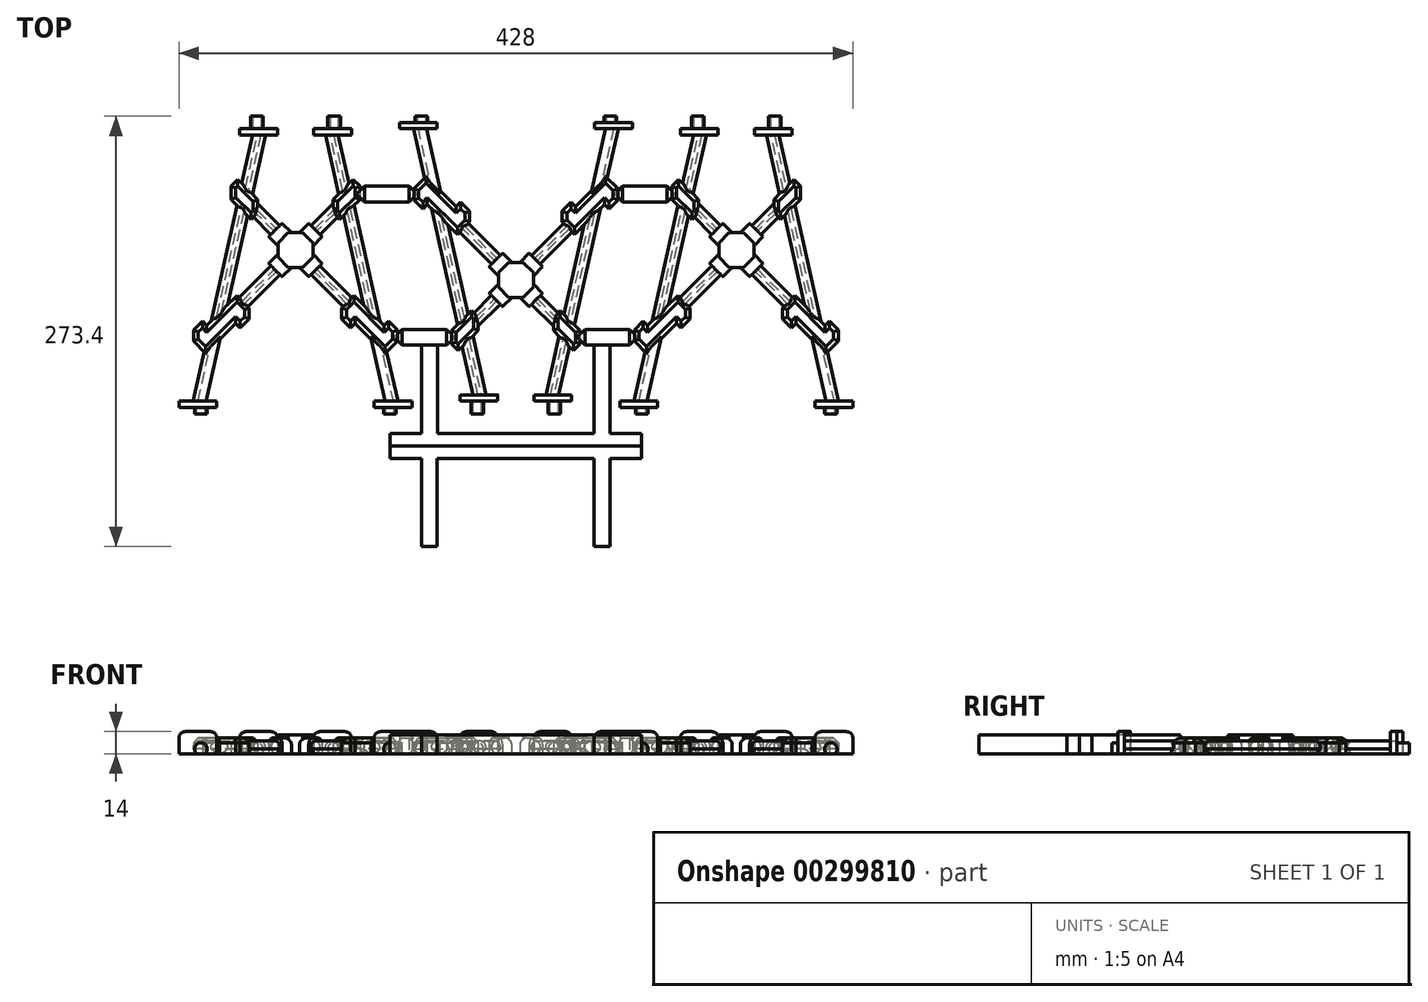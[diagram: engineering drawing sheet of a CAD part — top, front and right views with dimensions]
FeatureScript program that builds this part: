
annotation { "Feature Type Name" : "Feature", "Feature Type Description" : "" }
export const myFeature = defineFeature(function(context is Context, id is Id, definition is map)
    precondition{}
    {
        {
            var Q0;
            Q0=qCreatedBy(makeId("Front.planeOp"),FACE);
            var sketch = newSketch(context, id + "F0", { "sketchPlane" : qUnion([Q0])});
            skLineSegment(sketch, "E0", {"start": v(0, 0) * mm, "end": v(0, 65.95) * mm});
            skSolve(sketch);
        }
        {
            var Q0;
            Q0=qCreatedBy(makeId("Top.planeOp"),FACE);
            var sketch = newSketch(context, id + "F1", { "sketchPlane" : qUnion([Q0])});
            skLineSegment(sketch, "E1", {"start": v(26.5, 176.13) * mm, "end": v(65.92, 0) * mm});
            skLineSegment(sketch, "E2", {"start": v(18.1, 177) * mm, "end": v(27.88, 133.35) * mm});
            skLineSegment(sketch, "E3", {"start": v(43.95, 61.52) * mm, "end": v(5.66, 99.81) * mm});
            skLineSegment(sketch, "E4", {"start": v(47.21, 46.95) * mm, "end": v(0, 94.16) * mm});
            skLineSegment(sketch, "E5", {"start": v(43.95, 61.52) * mm, "end": v(57.71, 0.03) * mm});
            skLineSegment(sketch, "E6", {"start": v(5.66, 99.81) * mm, "end": v(29.95, 124.1) * mm});
            skLineSegment(sketch, "E7", {"start": v(0, 105.47) * mm, "end": v(27.88, 133.35) * mm});
            skLineSegment(sketch, "E8", {"start": v(0, 94.16) * mm, "end": v(0, 105.47) * mm});
            skLineSegment(sketch, "E9", {"start": v(18.1, 177) * mm, "end": v(26.5, 176.13) * mm});
            skLineSegment(sketch, "E10", {"start": v(57.71, 0.03) * mm, "end": v(65.92, 0) * mm});
            skLineSegment(sketch, "E11.trimOffspring", {"start": v(29.95, 124.1) * mm, "end": v(43.95, 61.52) * mm});
            skLineSegment(sketch, "E12.trimOffspring", {"start": v(47.21, 46.95) * mm, "end": v(57.71, 0.03) * mm});
            skLineSegment(sketch, "E13.MirrorCS", {"start": v(-43.95, 61.52) * mm, "end": v(-5.66, 99.81) * mm});
            skLineSegment(sketch, "E14.MirrorCS", {"start": v(-47.21, 46.95) * mm, "end": v(0, 94.16) * mm});
            skLineSegment(sketch, "E15.MirrorCS", {"start": v(-47.21, 46.95) * mm, "end": v(-57.71, 0.03) * mm});
            skLineSegment(sketch, "E16.MirrorCS", {"start": v(-18.1, 177) * mm, "end": v(-26.5, 176.13) * mm});
            skLineSegment(sketch, "E17.MirrorCS", {"start": v(-26.5, 176.13) * mm, "end": v(-65.92, 0) * mm});
            skLineSegment(sketch, "E18.MirrorCS", {"start": v(-18.1, 177) * mm, "end": v(-27.88, 133.35) * mm});
            skLineSegment(sketch, "E19.MirrorCS", {"start": v(-43.95, 61.52) * mm, "end": v(-57.71, 0.03) * mm});
            skLineSegment(sketch, "E20.MirrorCS", {"start": v(-5.66, 99.81) * mm, "end": v(-29.95, 124.1) * mm});
            skLineSegment(sketch, "E21.MirrorCS", {"start": v(0, 105.47) * mm, "end": v(-27.88, 133.35) * mm});
            skLineSegment(sketch, "E22.MirrorCS", {"start": v(-57.71, 0.03) * mm, "end": v(-65.92, 0) * mm});
            skLineSegment(sketch, "E23.MirrorCS", {"start": v(-29.95, 124.1) * mm, "end": v(-43.95, 61.52) * mm});
            skSolve(sketch);
        }
        {
            var Q0;
            Q0 = qSketchRegion(id + "F1", true);
            extrude(context, id + "F2", {"entities" : qUnion([Q0]), "depth" : 8 * mm});
        }
        {
            var Q0;
            Q0=qCreatedBy(makeId("Top.planeOp"),FACE);
            var sketch = newSketch(context, id + "F3", { "sketchPlane" : qUnion([Q0])});
            skLineSegment(sketch, "E24", {"start": v(0, 0) * mm, "end": v(50, 0) * mm});
            skLineSegment(sketch, "E25.bottom", {"start": v(50, 0) * mm, "end": v(74, 0) * mm});
            skLineSegment(sketch, "E25.top", {"start": v(50, 4) * mm, "end": v(74, 4) * mm});
            skLineSegment(sketch, "E25.left", {"start": v(50, 0) * mm, "end": v(50, 4) * mm});
            skLineSegment(sketch, "E25.right", {"start": v(74, 0) * mm, "end": v(74, 4) * mm});
            skLineSegment(sketch, "E26", {"start": v(0, 0) * mm, "end": v(0, 177) * mm});
            skLineSegment(sketch, "E27", {"start": v(0, 177) * mm, "end": v(11.5, 177) * mm});
            skLineSegment(sketch, "E28.bottom", {"start": v(11.5, 177) * mm, "end": v(35.5, 177) * mm});
            skLineSegment(sketch, "E28.top", {"start": v(11.5, 173) * mm, "end": v(35.5, 173) * mm});
            skLineSegment(sketch, "E28.left", {"start": v(11.5, 177) * mm, "end": v(11.5, 173) * mm});
            skLineSegment(sketch, "E28.right", {"start": v(35.5, 177) * mm, "end": v(35.5, 173) * mm});
            skLineSegment(sketch, "E29.MirrorCS", {"start": v(-11.5, 177) * mm, "end": v(-35.5, 177) * mm});
            skLineSegment(sketch, "E30.MirrorCS", {"start": v(-11.5, 173) * mm, "end": v(-35.5, 173) * mm});
            skLineSegment(sketch, "E31.MirrorCS", {"start": v(-35.5, 177) * mm, "end": v(-35.5, 173) * mm});
            skLineSegment(sketch, "E32.MirrorCS", {"start": v(-11.5, 177) * mm, "end": v(-11.5, 173) * mm});
            skLineSegment(sketch, "E33.MirrorCS", {"start": v(-50, 0) * mm, "end": v(-50, 4) * mm});
            skLineSegment(sketch, "E34.MirrorCS", {"start": v(-50, 0) * mm, "end": v(-74, 0) * mm});
            skLineSegment(sketch, "E35.MirrorCS", {"start": v(-50, 4) * mm, "end": v(-74, 4) * mm});
            skLineSegment(sketch, "E36.MirrorCS", {"start": v(-74, 0) * mm, "end": v(-74, 4) * mm});
            skSolve(sketch);
        }
        {
            var Q0;
            Q0 = qSketchRegion(id + "F3", true);
            extrude(context, id + "F4", {"entities" : qUnion([Q0]), "operationType" : NewBodyOperationType.ADD, "depth" : 14 * mm});
        }
        {
            var Q0;
            Q0=makeQuery(id+"F4.opExtrude","SWEPT_FACE",FACE,{"disambiguationData":[OSD([sQuery(id+"F3.wireOp",EDGE,"E25.bottom")])]});
            var sketch = newSketch(context, id + "F5", { "sketchPlane" : qUnion([Q0])});
            skPoint(sketch, "E37.endSnap0", {"position": v(50, 7) * mm});
            skLineSegment(sketch, "E38", {"start": v(60, 0) * mm, "end": v(60, 3) * mm});
            skArc(sketch, "E39", {"start": v(62.65, 0) * mm, "mid": v(60, 7) * mm, "end": v(57.35, 0) * mm});
            skLineSegment(sketch, "E40", {"start": v(57.35, 0) * mm, "end": v(62.65, 0) * mm});
            skLineSegment(sketch, "E41.MirrorCS", {"start": v(-57.35, 0) * mm, "end": v(-62.65, 0) * mm});
            skLineSegment(sketch, "E42.MirrorCS", {"start": v(-60, 0) * mm, "end": v(-60, 3) * mm});
            skArc(sketch, "E43.MirrorCS", {"start": v(-62.65, 0) * mm, "mid": v(-60, 7) * mm, "end": v(-57.35, 0) * mm});
            skPoint(sketch, "E44.MirrorP", {"position": v(-50, 7) * mm});
            skSolve(sketch);
        }
        {
            var Q0;
            Q0 = qSketchRegion(id + "F5", true);
            extrude(context, id + "F6", {"entities" : qUnion([Q0]), "operationType" : NewBodyOperationType.ADD, "depth" : 4 * mm});
        }
        {
            var Q0;
            Q0=makeQuery(id+"F4.opExtrude","SWEPT_FACE",FACE,{"disambiguationData":[OSD([sQuery(id+"F3.wireOp",EDGE,"E29.MirrorCS")])]});
            var sketch = newSketch(context, id + "F7", { "sketchPlane" : qUnion([Q0])});
            skArc(sketch, "E45", {"start": v(27.15, 0) * mm, "mid": v(24.5, 7) * mm, "end": v(21.85, 0) * mm});
            skLineSegment(sketch, "E46", {"start": v(21.85, 0) * mm, "end": v(27.15, 0) * mm});
            skArc(sketch, "E47.MirrorCS", {"start": v(-27.15, 0) * mm, "mid": v(-24.5, 7) * mm, "end": v(-21.85, 0) * mm});
            skLineSegment(sketch, "E48.MirrorCS", {"start": v(-21.85, 0) * mm, "end": v(-27.15, 0) * mm});
            skSolve(sketch);
        }
        {
            var Q0;
            Q0 = qSketchRegion(id + "F7", true);
            extrude(context, id + "F8", {"entities" : qUnion([Q0]), "operationType" : NewBodyOperationType.ADD, "depth" : 8 * mm});
        }
        {
            var Q0;
            Q0=qCreatedBy(makeId("Top.planeOp"),FACE);
            var sketch = newSketch(context, id + "F9", { "sketchPlane" : qUnion([Q0])});
            skLineSegment(sketch, "E49.bottom", {"start": v(8.49, 83.04) * mm, "end": v(0, 91.52) * mm});
            skLineSegment(sketch, "E49.top", {"start": v(16.97, 91.52) * mm, "end": v(8.49, 100) * mm});
            skLineSegment(sketch, "E49.left", {"start": v(8.49, 83.04) * mm, "end": v(16.97, 91.52) * mm});
            skLineSegment(sketch, "E49.right", {"start": v(-16.97, 108.5) * mm, "end": v(-8.49, 116.98) * mm});
            skPoint(sketch, "E49.middle", {"position": v(0, 100) * mm});
            skLineSegment(sketch, "E50.bottom", {"start": v(16.97, 108.5) * mm, "end": v(8.49, 116.98) * mm});
            skLineSegment(sketch, "E50.top", {"start": v(-8.49, 83.04) * mm, "end": v(-16.97, 91.52) * mm});
            skLineSegment(sketch, "E50.left", {"start": v(16.97, 108.5) * mm, "end": v(8.49, 100) * mm});
            skLineSegment(sketch, "E50.right", {"start": v(8.49, 116.98) * mm, "end": v(0, 108.5) * mm});
            skLineSegment(sketch, "E51.trimOffspring", {"start": v(0, 108.5) * mm, "end": v(-8.49, 116.98) * mm});
            skLineSegment(sketch, "E52.trimOffspring", {"start": v(-8.49, 100) * mm, "end": v(-16.97, 91.52) * mm});
            skLineSegment(sketch, "E53.trimOffspring", {"start": v(-8.49, 100) * mm, "end": v(-16.97, 108.5) * mm});
            skLineSegment(sketch, "E54.trimOffspring", {"start": v(0, 91.52) * mm, "end": v(-8.49, 83.04) * mm});
            skSolve(sketch);
        }
        {
            var Q0;
            Q0 = qSketchRegion(id + "F9", true);
            extrude(context, id + "F10", {"entities" : qUnion([Q0]), "operationType" : NewBodyOperationType.ADD, "depth" : 10 * mm});
        }
        {
            var Q0;
            Q0=qCreatedBy(makeId("Top.planeOp"),FACE);
            var sketch = newSketch(context, id + "F11", { "sketchPlane" : qUnion([Q0])});
            skLineSegment(sketch, "E55.bottom", {"start": v(35.07, 50.59) * mm, "end": v(29.41, 56.25) * mm});
            skLineSegment(sketch, "E55.top", {"start": v(64.77, 49.18) * mm, "end": v(59.11, 54.83) * mm});
            skLineSegment(sketch, "E55.right", {"start": v(29.41, 63.32) * mm, "end": v(37.2, 71.1) * mm});
            skPoint(sketch, "E55.middle", {"position": v(42.38, 57.42) * mm});
            skLineSegment(sketch, "E56", {"start": v(64.77, 42.1) * mm, "end": v(64.77, 49.18) * mm});
            skLineSegment(sketch, "E57", {"start": v(29.41, 56.25) * mm, "end": v(29.41, 63.32) * mm});
            skLineSegment(sketch, "E58", {"start": v(59.11, 54.83) * mm, "end": v(56.29, 52) * mm});
            skLineSegment(sketch, "E59", {"start": v(56.29, 52) * mm, "end": v(37.2, 71.1) * mm});
            skLineSegment(sketch, "E60", {"start": v(29.41, 56.25) * mm, "end": v(35.07, 50.59) * mm});
            skLineSegment(sketch, "E61", {"start": v(35.07, 50.59) * mm, "end": v(37.9, 53.42) * mm});
            skLineSegment(sketch, "E62", {"start": v(37.9, 53.42) * mm, "end": v(57, 34.33) * mm});
            skPoint(sketch, "E63.orphan", {"position": v(25.88, 59.78) * mm});
            skPoint(sketch, "E64.orphan", {"position": v(40.02, 73.92) * mm});
            skPoint(sketch, "E65.orphan", {"position": v(44.74, 40.93) * mm});
            skLineSegment(sketch, "E66", {"start": v(57, 34.33) * mm, "end": v(64.77, 42.1) * mm});
            skLineSegment(sketch, "E67.MirrorCS", {"start": v(-59.11, 54.83) * mm, "end": v(-56.29, 52) * mm});
            skLineSegment(sketch, "E68.MirrorCS", {"start": v(-35.07, 50.59) * mm, "end": v(-37.9, 53.42) * mm});
            skLineSegment(sketch, "E69.MirrorCS", {"start": v(-64.77, 49.18) * mm, "end": v(-59.11, 54.83) * mm});
            skLineSegment(sketch, "E70.MirrorCS", {"start": v(-35.07, 50.59) * mm, "end": v(-29.41, 56.25) * mm});
            skLineSegment(sketch, "E71.MirrorCS", {"start": v(-29.41, 56.25) * mm, "end": v(-29.41, 63.32) * mm});
            skPoint(sketch, "E72.MirrorP", {"position": v(-25.88, 59.78) * mm});
            skPoint(sketch, "E73.MirrorP", {"position": v(-42.38, 57.42) * mm});
            skLineSegment(sketch, "E74.MirrorCS", {"start": v(-37.9, 53.42) * mm, "end": v(-57, 34.33) * mm});
            skPoint(sketch, "E75.MirrorP", {"position": v(-40.02, 73.92) * mm});
            skPoint(sketch, "E76.MirrorP", {"position": v(-44.74, 40.93) * mm});
            skLineSegment(sketch, "E77.MirrorCS", {"start": v(-64.77, 42.1) * mm, "end": v(-64.77, 49.18) * mm});
            skLineSegment(sketch, "E78.MirrorCS", {"start": v(-29.41, 56.25) * mm, "end": v(-35.07, 50.59) * mm});
            skLineSegment(sketch, "E79.MirrorCS", {"start": v(-29.41, 63.32) * mm, "end": v(-37.2, 71.1) * mm});
            skLineSegment(sketch, "E80.MirrorCS", {"start": v(-57, 34.33) * mm, "end": v(-64.77, 42.1) * mm});
            skLineSegment(sketch, "E81.MirrorCS", {"start": v(-56.29, 52) * mm, "end": v(-37.2, 71.1) * mm});
            skSolve(sketch);
        }
        {
            var Q0;
            Q0 = qSketchRegion(id + "F11", true);
            extrude(context, id + "F12", {"entities" : qUnion([Q0]), "operationType" : NewBodyOperationType.ADD, "depth" : 10 * mm});
        }
        {
            var Q0;
            Q0=qCreatedBy(makeId("Top.planeOp"),FACE);
            var sketch = newSketch(context, id + "F13", { "sketchPlane" : qUnion([Q0])});
            skLineSegment(sketch, "E82", {"start": v(23.9, 132.15) * mm, "end": v(36.63, 144.88) * mm});
            skLineSegment(sketch, "E83", {"start": v(23.9, 123.67) * mm, "end": v(28.15, 119.43) * mm});
            skLineSegment(sketch, "E84", {"start": v(28.15, 119.43) * mm, "end": v(40.87, 132.15) * mm});
            skLineSegment(sketch, "E85", {"start": v(40.87, 140.64) * mm, "end": v(36.63, 144.88) * mm});
            skLineSegment(sketch, "E86", {"start": v(40.87, 140.64) * mm, "end": v(40.87, 132.15) * mm});
            skLineSegment(sketch, "E87", {"start": v(23.9, 123.67) * mm, "end": v(23.9, 132.15) * mm});
            skPoint(sketch, "E88.orphan", {"position": v(45.12, 136.4) * mm});
            skPoint(sketch, "E89.orphan", {"position": v(19.66, 127.91) * mm});
            skLineSegment(sketch, "E90.MirrorCS", {"start": v(-23.9, 123.67) * mm, "end": v(-23.9, 132.15) * mm});
            skPoint(sketch, "E91.MirrorP", {"position": v(-45.12, 136.4) * mm});
            skPoint(sketch, "E92.MirrorP", {"position": v(-19.66, 127.91) * mm});
            skLineSegment(sketch, "E93.MirrorCS", {"start": v(-40.87, 140.64) * mm, "end": v(-40.87, 132.15) * mm});
            skLineSegment(sketch, "E94.MirrorCS", {"start": v(-28.15, 119.43) * mm, "end": v(-40.87, 132.15) * mm});
            skLineSegment(sketch, "E95.MirrorCS", {"start": v(-23.9, 132.15) * mm, "end": v(-36.63, 144.88) * mm});
            skLineSegment(sketch, "E96.MirrorCS", {"start": v(-23.9, 123.67) * mm, "end": v(-28.15, 119.43) * mm});
            skLineSegment(sketch, "E97.MirrorCS", {"start": v(-40.87, 140.64) * mm, "end": v(-36.63, 144.88) * mm});
            skSolve(sketch);
        }
        {
            var Q0;
            Q0 = qSketchRegion(id + "F13", true);
            extrude(context, id + "F14", {"entities" : qUnion([Q0]), "operationType" : NewBodyOperationType.ADD, "depth" : 10 * mm});
        }
        {
            var Q0;
            {var subQ0=sQuery(id+"F1.wireOp",EDGE,"E17.MirrorCS");Q0=makeQuery(id+"F12.boolean.opBoolean","SPLIT",EDGE,{"disambiguationData":[TD([makeQuery(id+"F4.opExtrude","SWEPT_FACE",FACE,{"disambiguationData":[OSD([sQuery(id+"F3.wireOp",EDGE,"E30.MirrorCS")])]})])],"derivedFrom":makeQuery(id+"F2.opExtrude","CAP_EDGE",EDGE,{"disambiguationData":[OSD([subQ0])],"isStart":false})});}
            var Q1;
            Q1=makeQuery(id+"F2.opExtrude","CAP_EDGE",EDGE,{"disambiguationData":[OSD([sQuery(id+"F1.wireOp",EDGE,"E23.MirrorCS")])],"isStart":false});
            var Q2;
            Q2=makeQuery(id+"F2.opExtrude","CAP_EDGE",EDGE,{"disambiguationData":[OSD([sQuery(id+"F1.wireOp",EDGE,"E18.MirrorCS")])],"isStart":false});
            var Q3;
            Q3=makeQuery(id+"F2.opExtrude","CAP_EDGE",EDGE,{"disambiguationData":[OSD([sQuery(id+"F1.wireOp",EDGE,"E21.MirrorCS")])],"isStart":false});
            var Q4;
            Q4=makeQuery(id+"F2.opExtrude","CAP_EDGE",EDGE,{"disambiguationData":[OSD([sQuery(id+"F1.wireOp",EDGE,"E20.MirrorCS")])],"isStart":false});
            var Q5;
            Q5=makeQuery(id+"F2.opExtrude","CAP_EDGE",EDGE,{"disambiguationData":[OSD([sQuery(id+"F1.wireOp",EDGE,"E7")])],"isStart":false});
            var Q6;
            Q6=makeQuery(id+"F2.opExtrude","CAP_EDGE",EDGE,{"disambiguationData":[OSD([sQuery(id+"F1.wireOp",EDGE,"E2")])],"isStart":false});
            var Q7;
            {var subQ0=sQuery(id+"F1.wireOp",EDGE,"E1");Q7=makeQuery(id+"F12.boolean.opBoolean","SPLIT",EDGE,{"disambiguationData":[TD([makeQuery(id+"F4.opExtrude","SWEPT_FACE",FACE,{"disambiguationData":[OSD([sQuery(id+"F3.wireOp",EDGE,"E28.top")])]})])],"derivedFrom":makeQuery(id+"F2.opExtrude","CAP_EDGE",EDGE,{"disambiguationData":[OSD([subQ0])],"isStart":false})});}
            var Q8;
            Q8=makeQuery(id+"F2.opExtrude","CAP_EDGE",EDGE,{"disambiguationData":[OSD([sQuery(id+"F1.wireOp",EDGE,"E11.trimOffspring")])],"isStart":false});
            var Q9;
            Q9=makeQuery(id+"F2.opExtrude","CAP_EDGE",EDGE,{"disambiguationData":[OSD([sQuery(id+"F1.wireOp",EDGE,"E12.trimOffspring")])],"isStart":false});
            var Q10;
            {var subQ0=sQuery(id+"F1.wireOp",EDGE,"E1");Q10=makeQuery(id+"F12.boolean.opBoolean","SPLIT",EDGE,{"disambiguationData":[TD([makeQuery(id+"F4.opExtrude","SWEPT_FACE",FACE,{"disambiguationData":[OSD([sQuery(id+"F3.wireOp",EDGE,"E25.top")])]})])],"derivedFrom":makeQuery(id+"F2.opExtrude","CAP_EDGE",EDGE,{"disambiguationData":[OSD([subQ0])],"isStart":false})});}
            var Q11;
            {var subQ0=sQuery(id+"F1.wireOp",EDGE,"E17.MirrorCS");Q11=makeQuery(id+"F12.boolean.opBoolean","SPLIT",EDGE,{"disambiguationData":[TD([makeQuery(id+"F4.opExtrude","SWEPT_FACE",FACE,{"disambiguationData":[OSD([sQuery(id+"F3.wireOp",EDGE,"E35.MirrorCS")])]})])],"derivedFrom":makeQuery(id+"F2.opExtrude","CAP_EDGE",EDGE,{"disambiguationData":[OSD([subQ0])],"isStart":false})});}
            var Q12;
            Q12=makeQuery(id+"F2.opExtrude","CAP_EDGE",EDGE,{"disambiguationData":[OSD([sQuery(id+"F1.wireOp",EDGE,"E14.MirrorCS")])],"isStart":false});
            var Q13;
            Q13=makeQuery(id+"F2.opExtrude","CAP_EDGE",EDGE,{"disambiguationData":[OSD([sQuery(id+"F1.wireOp",EDGE,"E13.MirrorCS")])],"isStart":false});
            var Q14;
            Q14=makeQuery(id+"F2.opExtrude","CAP_EDGE",EDGE,{"disambiguationData":[OSD([sQuery(id+"F1.wireOp",EDGE,"E4")])],"isStart":false});
            var Q15;
            Q15=makeQuery(id+"F2.opExtrude","CAP_EDGE",EDGE,{"disambiguationData":[OSD([sQuery(id+"F1.wireOp",EDGE,"E3")])],"isStart":false});
            var Q16;
            Q16=makeQuery(id+"F2.opExtrude","CAP_EDGE",EDGE,{"disambiguationData":[OSD([sQuery(id+"F1.wireOp",EDGE,"E6")])],"isStart":false});
            var Q17;
            Q17=makeQuery(id+"F2.opExtrude","CAP_EDGE",EDGE,{"disambiguationData":[OSD([sQuery(id+"F1.wireOp",EDGE,"E19.MirrorCS")])],"isStart":false});
            var Q18;
            {var subQ0=sQuery(id+"F9.wireOp",EDGE,"E50.left");Q18=makeQuery(id+"F10.opExtrude","CAP_EDGE",EDGE,{"disambiguationData":[OSD([subQ0]),TDD([makeQuery(id+"F9.imprint","IMPRINT",EDGE,{"disambiguationData":[TD([[makeQuery(id+"F9.imprint","INTERSECT",VERTEX,{"derivedFrom":[sQuery(id+"F9.wireOp",EDGE,"E50.top"),subQ0]}),1.0]])],"derivedFrom":subQ0})])],"isStart":false});}
            var Q19;
            {var subQ0=sQuery(id+"F9.wireOp",EDGE,"E50.right");Q19=makeQuery(id+"F10.opExtrude","CAP_EDGE",EDGE,{"disambiguationData":[OSD([subQ0]),TDD([makeQuery(id+"F9.imprint","IMPRINT",EDGE,{"disambiguationData":[TD([[makeQuery(id+"F9.imprint","INTERSECT",VERTEX,{"derivedFrom":[sQuery(id+"F9.wireOp",EDGE,"E50.top"),subQ0]}),1.0]])],"derivedFrom":subQ0})])],"isStart":false});}
            var Q20;
            {var subQ0=sQuery(id+"F9.wireOp",EDGE,"E49.bottom");Q20=makeQuery(id+"F10.opExtrude","CAP_EDGE",EDGE,{"disambiguationData":[OSD([subQ0]),TDD([makeQuery(id+"F9.imprint","IMPRINT",EDGE,{"disambiguationData":[TD([[makeQuery(id+"F9.imprint","INTERSECT",VERTEX,{"derivedFrom":[subQ0,sQuery(id+"F9.wireOp",EDGE,"E49.right")]}),1.0]])],"derivedFrom":subQ0})])],"isStart":false});}
            var Q21;
            {var subQ0=sQuery(id+"F9.wireOp",EDGE,"E49.top");Q21=makeQuery(id+"F10.opExtrude","CAP_EDGE",EDGE,{"disambiguationData":[OSD([subQ0]),TDD([makeQuery(id+"F9.imprint","IMPRINT",EDGE,{"disambiguationData":[TD([[makeQuery(id+"F9.imprint","INTERSECT",VERTEX,{"derivedFrom":[subQ0,sQuery(id+"F9.wireOp",EDGE,"E49.right")]}),1.0]])],"derivedFrom":subQ0})])],"isStart":false});}
            var Q22;
            {var subQ0=sQuery(id+"F9.wireOp",EDGE,"E50.right");Q22=makeQuery(id+"F10.opExtrude","CAP_EDGE",EDGE,{"disambiguationData":[OSD([subQ0]),TDD([makeQuery(id+"F9.imprint","IMPRINT",EDGE,{"disambiguationData":[TD([[makeQuery(id+"F9.imprint","INTERSECT",VERTEX,{"derivedFrom":[sQuery(id+"F9.wireOp",EDGE,"E50.bottom"),subQ0]}),-1.0]])],"derivedFrom":subQ0})])],"isStart":false});}
            var Q23;
            {var subQ0=sQuery(id+"F9.wireOp",EDGE,"E50.left");Q23=makeQuery(id+"F10.opExtrude","CAP_EDGE",EDGE,{"disambiguationData":[OSD([subQ0]),TDD([makeQuery(id+"F9.imprint","IMPRINT",EDGE,{"disambiguationData":[TD([[makeQuery(id+"F9.imprint","INTERSECT",VERTEX,{"derivedFrom":[sQuery(id+"F9.wireOp",EDGE,"E50.bottom"),subQ0]}),-1.0]])],"derivedFrom":subQ0})])],"isStart":false});}
            var Q24;
            {var subQ0=sQuery(id+"F9.wireOp",EDGE,"E49.top");Q24=makeQuery(id+"F10.opExtrude","CAP_EDGE",EDGE,{"disambiguationData":[OSD([subQ0]),TDD([makeQuery(id+"F9.imprint","IMPRINT",EDGE,{"disambiguationData":[TD([[makeQuery(id+"F9.imprint","INTERSECT",VERTEX,{"derivedFrom":[subQ0,sQuery(id+"F9.wireOp",EDGE,"E49.left")]}),-1.0]])],"derivedFrom":subQ0})])],"isStart":false});}
            var Q25;
            {var subQ0=sQuery(id+"F9.wireOp",EDGE,"E49.bottom");Q25=makeQuery(id+"F10.opExtrude","CAP_EDGE",EDGE,{"disambiguationData":[OSD([subQ0]),TDD([makeQuery(id+"F9.imprint","IMPRINT",EDGE,{"disambiguationData":[TD([[makeQuery(id+"F9.imprint","INTERSECT",VERTEX,{"derivedFrom":[subQ0,sQuery(id+"F9.wireOp",EDGE,"E49.left")]}),-1.0]])],"derivedFrom":subQ0})])],"isStart":false});}
            var Q26;
            Q26=makeQuery(id+"F4.opExtrude","CAP_EDGE",EDGE,{"disambiguationData":[OSD([sQuery(id+"F3.wireOp",EDGE,"E32.MirrorCS")])],"isStart":false});
            var Q27;
            Q27=makeQuery(id+"F4.opExtrude","CAP_EDGE",EDGE,{"disambiguationData":[OSD([sQuery(id+"F3.wireOp",EDGE,"E31.MirrorCS")])],"isStart":false});
            var Q28;
            Q28=makeQuery(id+"F4.opExtrude","CAP_EDGE",EDGE,{"disambiguationData":[OSD([sQuery(id+"F3.wireOp",EDGE,"E28.left")])],"isStart":false});
            var Q29;
            Q29=makeQuery(id+"F4.opExtrude","CAP_EDGE",EDGE,{"disambiguationData":[OSD([sQuery(id+"F3.wireOp",EDGE,"E28.right")])],"isStart":false});
            var Q30;
            Q30=makeQuery(id+"F4.opExtrude","CAP_EDGE",EDGE,{"disambiguationData":[OSD([sQuery(id+"F3.wireOp",EDGE,"E25.left")])],"isStart":false});
            var Q31;
            Q31=makeQuery(id+"F4.opExtrude","CAP_EDGE",EDGE,{"disambiguationData":[OSD([sQuery(id+"F3.wireOp",EDGE,"E25.right")])],"isStart":false});
            var Q32;
            Q32=makeQuery(id+"F4.opExtrude","CAP_EDGE",EDGE,{"disambiguationData":[OSD([sQuery(id+"F3.wireOp",EDGE,"E33.MirrorCS")])],"isStart":false});
            var Q33;
            Q33=makeQuery(id+"F4.opExtrude","CAP_EDGE",EDGE,{"disambiguationData":[OSD([sQuery(id+"F3.wireOp",EDGE,"E36.MirrorCS")])],"isStart":false});
            var Q34;
            Q34=makeQuery(id+"F10.opExtrude","CAP_EDGE",EDGE,{"disambiguationData":[OSD([sQuery(id+"F9.wireOp",EDGE,"E54.trimOffspring")])],"isStart":false});
            var Q35;
            Q35=makeQuery(id+"F10.opExtrude","CAP_EDGE",EDGE,{"disambiguationData":[OSD([sQuery(id+"F9.wireOp",EDGE,"E52.trimOffspring")])],"isStart":false});
            var Q36;
            Q36=makeQuery(id+"F10.opExtrude","CAP_EDGE",EDGE,{"disambiguationData":[OSD([sQuery(id+"F9.wireOp",EDGE,"E53.trimOffspring")])],"isStart":false});
            var Q37;
            Q37=makeQuery(id+"F10.opExtrude","CAP_EDGE",EDGE,{"disambiguationData":[OSD([sQuery(id+"F9.wireOp",EDGE,"E51.trimOffspring")])],"isStart":false});
            fillet(context, id + "F15", {"entities" : qUnion([Q0, Q1, Q2, Q3, Q4, Q5, Q6, Q7, Q8, Q9, Q10, Q11, Q12, Q13, Q14, Q15, Q16, Q17, Q18, Q19, Q20, Q21, Q22, Q23, Q24, Q25, Q26, Q27, Q28, Q29, Q30, Q31, Q32, Q33, Q34, Q35, Q36, Q37]), "radius" : 4 * mm, "tangentPropagation" : true, "allowEdgeOverflow" : false});
        }
        {
            var Q0;
            {var subQ0=sQuery(id+"F3.wireOp",EDGE,"E35.MirrorCS");var subQ2=sQuery(id+"F1.wireOp",EDGE,"E17.MirrorCS");Q0=makeQuery(id+"F12.boolean.opBoolean","SPLIT",EDGE,{"disambiguationData":[TD([makeQuery(id+"F4.opExtrude","SWEPT_FACE",FACE,{"disambiguationData":[OSD([subQ0])]})])],"derivedFrom":makeQuery(id+"F2.opExtrude","CAP_EDGE",EDGE,{"disambiguationData":[OSD([subQ2])],"isStart":true})});}
            var Q1;
            Q1=makeQuery(id+"F2.opExtrude","CAP_EDGE",EDGE,{"disambiguationData":[OSD([sQuery(id+"F1.wireOp",EDGE,"E19.MirrorCS")])],"isStart":true});
            var Q2;
            {var subQ1=sQuery(id+"F1.wireOp",EDGE,"E1");var subQ2=sQuery(id+"F3.wireOp",EDGE,"E28.top");Q2=makeQuery(id+"F12.boolean.opBoolean","SPLIT",EDGE,{"disambiguationData":[TD([makeQuery(id+"F4.opExtrude","SWEPT_FACE",FACE,{"disambiguationData":[OSD([subQ2])]})])],"derivedFrom":makeQuery(id+"F2.opExtrude","CAP_EDGE",EDGE,{"disambiguationData":[OSD([subQ1])],"isStart":true})});}
            var Q3;
            Q3=makeQuery(id+"F2.opExtrude","CAP_EDGE",EDGE,{"disambiguationData":[OSD([sQuery(id+"F1.wireOp",EDGE,"E11.trimOffspring")])],"isStart":true});
            var Q4;
            Q4=makeQuery(id+"F2.opExtrude","CAP_EDGE",EDGE,{"disambiguationData":[OSD([sQuery(id+"F1.wireOp",EDGE,"E6")])],"isStart":true});
            var Q5;
            Q5=makeQuery(id+"F2.opExtrude","CAP_EDGE",EDGE,{"disambiguationData":[OSD([sQuery(id+"F1.wireOp",EDGE,"E7")])],"isStart":true});
            var Q6;
            Q6=makeQuery(id+"F2.opExtrude","CAP_EDGE",EDGE,{"disambiguationData":[OSD([sQuery(id+"F1.wireOp",EDGE,"E2")])],"isStart":true});
            var Q7;
            Q7=makeQuery(id+"F2.opExtrude","CAP_EDGE",EDGE,{"disambiguationData":[OSD([sQuery(id+"F1.wireOp",EDGE,"E18.MirrorCS")])],"isStart":true});
            var Q8;
            Q8=makeQuery(id+"F2.opExtrude","CAP_EDGE",EDGE,{"disambiguationData":[OSD([sQuery(id+"F1.wireOp",EDGE,"E21.MirrorCS")])],"isStart":true});
            var Q9;
            Q9=makeQuery(id+"F2.opExtrude","CAP_EDGE",EDGE,{"disambiguationData":[OSD([sQuery(id+"F1.wireOp",EDGE,"E20.MirrorCS")])],"isStart":true});
            var Q10;
            Q10=makeQuery(id+"F2.opExtrude","CAP_EDGE",EDGE,{"disambiguationData":[OSD([sQuery(id+"F1.wireOp",EDGE,"E23.MirrorCS")])],"isStart":true});
            var Q11;
            Q11=makeQuery(id+"F2.opExtrude","CAP_EDGE",EDGE,{"disambiguationData":[OSD([sQuery(id+"F1.wireOp",EDGE,"E13.MirrorCS")])],"isStart":true});
            var Q12;
            Q12=makeQuery(id+"F2.opExtrude","CAP_EDGE",EDGE,{"disambiguationData":[OSD([sQuery(id+"F1.wireOp",EDGE,"E14.MirrorCS")])],"isStart":true});
            var Q13;
            Q13=makeQuery(id+"F2.opExtrude","CAP_EDGE",EDGE,{"disambiguationData":[OSD([sQuery(id+"F1.wireOp",EDGE,"E4")])],"isStart":true});
            var Q14;
            Q14=makeQuery(id+"F2.opExtrude","CAP_EDGE",EDGE,{"disambiguationData":[OSD([sQuery(id+"F1.wireOp",EDGE,"E3")])],"isStart":true});
            var Q15;
            {var subQ1=sQuery(id+"F3.wireOp",EDGE,"E30.MirrorCS");var subQ2=sQuery(id+"F1.wireOp",EDGE,"E17.MirrorCS");Q15=makeQuery(id+"F12.boolean.opBoolean","SPLIT",EDGE,{"disambiguationData":[TD([makeQuery(id+"F4.opExtrude","SWEPT_FACE",FACE,{"disambiguationData":[OSD([subQ1])]})])],"derivedFrom":makeQuery(id+"F2.opExtrude","CAP_EDGE",EDGE,{"disambiguationData":[OSD([subQ2])],"isStart":true})});}
            var Q16;
            Q16=makeQuery(id+"F2.opExtrude","CAP_EDGE",EDGE,{"disambiguationData":[OSD([sQuery(id+"F1.wireOp",EDGE,"E12.trimOffspring")])],"isStart":true});
            var Q17;
            {var subQ1=sQuery(id+"F1.wireOp",EDGE,"E1");var subQ2=sQuery(id+"F3.wireOp",EDGE,"E25.top");Q17=makeQuery(id+"F12.boolean.opBoolean","SPLIT",EDGE,{"disambiguationData":[TD([makeQuery(id+"F4.opExtrude","SWEPT_FACE",FACE,{"disambiguationData":[OSD([subQ2])]})])],"derivedFrom":makeQuery(id+"F2.opExtrude","CAP_EDGE",EDGE,{"disambiguationData":[OSD([subQ1])],"isStart":true})});}
            var Q18;
            Q18=makeQuery(id+"F12.opExtrude","CAP_FACE",FACE,{"disambiguationData":[OSD([sQuery(id+"F11.wireOp",EDGE,"E55.right"),sQuery(id+"F11.wireOp",EDGE,"E56"),sQuery(id+"F11.wireOp",EDGE,"E57"),sQuery(id+"F11.wireOp",EDGE,"E55.top"),sQuery(id+"F11.wireOp",EDGE,"E58"),sQuery(id+"F11.wireOp",EDGE,"E59"),sQuery(id+"F11.wireOp",EDGE,"E60"),sQuery(id+"F11.wireOp",EDGE,"E61"),sQuery(id+"F11.wireOp",EDGE,"E62"),sQuery(id+"F11.wireOp",EDGE,"E66")])],"isStart":false});
            var Q19;
            Q19=makeQuery(id+"F12.opExtrude","CAP_FACE",FACE,{"disambiguationData":[OSD([sQuery(id+"F11.wireOp",EDGE,"E67.MirrorCS"),sQuery(id+"F11.wireOp",EDGE,"E68.MirrorCS"),sQuery(id+"F11.wireOp",EDGE,"E71.MirrorCS"),sQuery(id+"F11.wireOp",EDGE,"E74.MirrorCS"),sQuery(id+"F11.wireOp",EDGE,"E77.MirrorCS"),sQuery(id+"F11.wireOp",EDGE,"E78.MirrorCS"),sQuery(id+"F11.wireOp",EDGE,"E79.MirrorCS"),sQuery(id+"F11.wireOp",EDGE,"E80.MirrorCS"),sQuery(id+"F11.wireOp",EDGE,"E81.MirrorCS"),sQuery(id+"F11.wireOp",EDGE,"E69.MirrorCS")])],"isStart":false});
            var Q20;
            Q20=makeQuery(id+"F14.opExtrude","CAP_FACE",FACE,{"disambiguationData":[OSD([sQuery(id+"F13.wireOp",EDGE,"E82"),sQuery(id+"F13.wireOp",EDGE,"E83"),sQuery(id+"F13.wireOp",EDGE,"E84"),sQuery(id+"F13.wireOp",EDGE,"E85"),sQuery(id+"F13.wireOp",EDGE,"E86"),sQuery(id+"F13.wireOp",EDGE,"E87")])],"isStart":false});
            var Q21;
            Q21=makeQuery(id+"F14.opExtrude","CAP_FACE",FACE,{"disambiguationData":[OSD([sQuery(id+"F13.wireOp",EDGE,"E90.MirrorCS"),sQuery(id+"F13.wireOp",EDGE,"E93.MirrorCS"),sQuery(id+"F13.wireOp",EDGE,"E94.MirrorCS"),sQuery(id+"F13.wireOp",EDGE,"E95.MirrorCS"),sQuery(id+"F13.wireOp",EDGE,"E96.MirrorCS"),sQuery(id+"F13.wireOp",EDGE,"E97.MirrorCS")])],"isStart":false});
            chamfer(context, id + "F16", {"entities" : qUnion([Q0, Q1, Q2, Q3, Q4, Q5, Q6, Q7, Q8, Q9, Q10, Q11, Q12, Q13, Q14, Q15, Q16, Q17, Q18, Q19, Q20, Q21]), "width" : 3 * mm, "tangentPropagation" : true});
        }
        {
            var Q0;
            Q0=qCreatedBy(makeId("Top.planeOp"),FACE);
            var sketch = newSketch(context, id + "F17", { "sketchPlane" : qUnion([Q0])});
            skCircle(sketch, "E98.cCircle", {"center": v(0, 100) * mm, "radius": 12 * mm, "construction": true});
            skPoint(sketch, "E98.cCircle.perimeterSnap0", {"position": v(5.67, 91.53) * mm});
            skPoint(sketch, "E98.cCircle.perimeterSnap1", {"position": v(1.98, 90) * mm});
            skLineSegment(sketch, "E98.0", {"start": v(4.6, 88.92) * mm, "end": v(-4.6, 88.92) * mm});
            skPoint(sketch, "E98.0.startSnap0", {"position": v(5.67, 91.53) * mm});
            skPoint(sketch, "E98.0.startSnap1", {"position": v(1.98, 90) * mm});
            skLineSegment(sketch, "E98.1", {"start": v(-4.6, 88.92) * mm, "end": v(-11.09, 95.42) * mm});
            skLineSegment(sketch, "E98.2", {"start": v(-11.09, 95.42) * mm, "end": v(-11.09, 104.6) * mm});
            skLineSegment(sketch, "E98.3", {"start": v(-11.09, 104.6) * mm, "end": v(-4.6, 111.1) * mm});
            skLineSegment(sketch, "E98.4", {"start": v(-4.6, 111.1) * mm, "end": v(4.6, 111.1) * mm});
            skLineSegment(sketch, "E98.5", {"start": v(4.6, 111.1) * mm, "end": v(11.09, 104.6) * mm});
            skLineSegment(sketch, "E98.6", {"start": v(11.09, 104.6) * mm, "end": v(11.09, 95.42) * mm});
            skLineSegment(sketch, "E98.7", {"start": v(11.09, 95.42) * mm, "end": v(4.6, 88.92) * mm});
            skLineSegment(sketch, "E99.0", {"start": v(1.98, 90) * mm, "end": v(4.6, 88.92) * mm, "construction": true});
            skLineSegment(sketch, "E100.0", {"start": v(4.6, 88.92) * mm, "end": v(5.67, 91.53) * mm, "construction": true});
            skSolve(sketch);
        }
        {
            var Q0;
            Q0 = qSketchRegion(id + "F17", true);
            extrude(context, id + "F18", {"entities" : qUnion([Q0]), "operationType" : NewBodyOperationType.ADD, "depth" : 12 * mm});
        }
        {
            var Q0;
            Q0=makeQuery(id+"F2.opExtrude","SWEPT_BODY",BODY,{"disambiguationData":[OSD([sQuery(id+"F1.wireOp",EDGE,"E1"),sQuery(id+"F1.wireOp",EDGE,"E2"),sQuery(id+"F1.wireOp",EDGE,"E3"),sQuery(id+"F1.wireOp",EDGE,"E4"),sQuery(id+"F1.wireOp",EDGE,"E6"),sQuery(id+"F1.wireOp",EDGE,"E7"),sQuery(id+"F1.wireOp",EDGE,"E9"),sQuery(id+"F1.wireOp",EDGE,"E10"),sQuery(id+"F1.wireOp",EDGE,"E11.trimOffspring"),sQuery(id+"F1.wireOp",EDGE,"E12.trimOffspring"),sQuery(id+"F1.wireOp",EDGE,"E13.MirrorCS"),sQuery(id+"F1.wireOp",EDGE,"E14.MirrorCS"),sQuery(id+"F1.wireOp",EDGE,"E16.MirrorCS"),sQuery(id+"F1.wireOp",EDGE,"E17.MirrorCS"),sQuery(id+"F1.wireOp",EDGE,"E18.MirrorCS"),sQuery(id+"F1.wireOp",EDGE,"E19.MirrorCS"),sQuery(id+"F1.wireOp",EDGE,"E20.MirrorCS"),sQuery(id+"F1.wireOp",EDGE,"E21.MirrorCS"),sQuery(id+"F1.wireOp",EDGE,"E22.MirrorCS"),sQuery(id+"F1.wireOp",EDGE,"E23.MirrorCS")])]});
            var Q1;
            Q1=sQuery(id+"F0.wireOp",EDGE,"E0");
            transform(context, id + "F19", {"entities" : qUnion([Q0]), "transformType" : TransformType.ROTATION, "transformAxis" : qUnion([Q1]), "angle" : 180 * degree, "makeCopy" : true});
        }
        {
            var Q0;
            Q0=makeQuery(id+"F19.opPattern","COPY",BODY,{"derivedFrom":makeQuery(id+"F2.opExtrude","SWEPT_BODY",BODY,{"disambiguationData":[OSD([sQuery(id+"F1.wireOp",EDGE,"E1"),sQuery(id+"F1.wireOp",EDGE,"E2"),sQuery(id+"F1.wireOp",EDGE,"E3"),sQuery(id+"F1.wireOp",EDGE,"E4"),sQuery(id+"F1.wireOp",EDGE,"E6"),sQuery(id+"F1.wireOp",EDGE,"E7"),sQuery(id+"F1.wireOp",EDGE,"E9"),sQuery(id+"F1.wireOp",EDGE,"E10"),sQuery(id+"F1.wireOp",EDGE,"E11.trimOffspring"),sQuery(id+"F1.wireOp",EDGE,"E12.trimOffspring"),sQuery(id+"F1.wireOp",EDGE,"E13.MirrorCS"),sQuery(id+"F1.wireOp",EDGE,"E14.MirrorCS"),sQuery(id+"F1.wireOp",EDGE,"E16.MirrorCS"),sQuery(id+"F1.wireOp",EDGE,"E17.MirrorCS"),sQuery(id+"F1.wireOp",EDGE,"E18.MirrorCS"),sQuery(id+"F1.wireOp",EDGE,"E19.MirrorCS"),sQuery(id+"F1.wireOp",EDGE,"E20.MirrorCS"),sQuery(id+"F1.wireOp",EDGE,"E21.MirrorCS"),sQuery(id+"F1.wireOp",EDGE,"E22.MirrorCS"),sQuery(id+"F1.wireOp",EDGE,"E23.MirrorCS")])]}),"instanceName":"1"});
            transform(context, id + "F20", {"entities" : qUnion([Q0]), "transformType" : TransformType.TRANSLATION_3D, "dx" : 140 * mm, "dy" : 181 * mm, "dz" : 0 * mm, "makeCopy" : false});
        }
        {
            var Q0;
            Q0=makeQuery(id+"F2.opExtrude","SWEPT_BODY",BODY,{"disambiguationData":[OSD([sQuery(id+"F1.wireOp",EDGE,"E1"),sQuery(id+"F1.wireOp",EDGE,"E2"),sQuery(id+"F1.wireOp",EDGE,"E3"),sQuery(id+"F1.wireOp",EDGE,"E4"),sQuery(id+"F1.wireOp",EDGE,"E6"),sQuery(id+"F1.wireOp",EDGE,"E7"),sQuery(id+"F1.wireOp",EDGE,"E9"),sQuery(id+"F1.wireOp",EDGE,"E10"),sQuery(id+"F1.wireOp",EDGE,"E11.trimOffspring"),sQuery(id+"F1.wireOp",EDGE,"E12.trimOffspring"),sQuery(id+"F1.wireOp",EDGE,"E13.MirrorCS"),sQuery(id+"F1.wireOp",EDGE,"E14.MirrorCS"),sQuery(id+"F1.wireOp",EDGE,"E16.MirrorCS"),sQuery(id+"F1.wireOp",EDGE,"E17.MirrorCS"),sQuery(id+"F1.wireOp",EDGE,"E18.MirrorCS"),sQuery(id+"F1.wireOp",EDGE,"E19.MirrorCS"),sQuery(id+"F1.wireOp",EDGE,"E20.MirrorCS"),sQuery(id+"F1.wireOp",EDGE,"E21.MirrorCS"),sQuery(id+"F1.wireOp",EDGE,"E22.MirrorCS"),sQuery(id+"F1.wireOp",EDGE,"E23.MirrorCS")])]});
            transform(context, id + "F21", {"entities" : qUnion([Q0]), "transformType" : TransformType.TRANSLATION_3D, "dx" : 280 * mm, "dy" : 0 * mm, "dz" : 0 * mm, "makeCopy" : true});
        }
        {
            var Q0;
            Q0=qCreatedBy(makeId("Top.planeOp"),FACE);
            var sketch = newSketch(context, id + "F22", { "sketchPlane" : qUnion([Q0])});
            skLineSegment(sketch, "E101.bottom", {"start": v(62.77, 49.6) * mm, "end": v(101.13, 49.6) * mm});
            skLineSegment(sketch, "E101.top", {"start": v(62.77, 39.6) * mm, "end": v(101.13, 39.6) * mm});
            skLineSegment(sketch, "E101.left", {"start": v(62.77, 49.6) * mm, "end": v(62.77, 39.6) * mm});
            skLineSegment(sketch, "E101.right", {"start": v(101.13, 49.6) * mm, "end": v(101.13, 39.6) * mm});
            skSolve(sketch);
        }
        {
            var Q0;
            Q0 = qSketchRegion(id + "F22", true);
            extrude(context, id + "F23", {"entities" : qUnion([Q0]), "depth" : 10 * mm, "offsetDistance" : 25 * mm});
        }
        {
            var Q0;
            Q0=makeQuery(id+"F23.opExtrude","SWEPT_EDGE",EDGE,{"disambiguationData":[OSD([sQuery(id+"F22.wireOp",EDGE,"E101.bottom"),sQuery(id+"F22.wireOp",EDGE,"E101.left")])]});
            var Q1;
            Q1=makeQuery(id+"F23.opExtrude","CAP_EDGE",EDGE,{"disambiguationData":[OSD([sQuery(id+"F22.wireOp",EDGE,"E101.left")])],"isStart":true});
            var Q2;
            Q2=makeQuery(id+"F23.opExtrude","SWEPT_EDGE",EDGE,{"disambiguationData":[OSD([sQuery(id+"F22.wireOp",EDGE,"E101.top"),sQuery(id+"F22.wireOp",EDGE,"E101.right")])]});
            var Q3;
            Q3=makeQuery(id+"F23.opExtrude","SWEPT_EDGE",EDGE,{"disambiguationData":[OSD([sQuery(id+"F22.wireOp",EDGE,"E101.bottom"),sQuery(id+"F22.wireOp",EDGE,"E101.right")])]});
            var Q4;
            Q4=makeQuery(id+"F23.opExtrude","CAP_EDGE",EDGE,{"disambiguationData":[OSD([sQuery(id+"F22.wireOp",EDGE,"E101.right")])],"isStart":true});
            var Q5;
            Q5=makeQuery(id+"F23.opExtrude","SWEPT_EDGE",EDGE,{"disambiguationData":[OSD([sQuery(id+"F22.wireOp",EDGE,"E101.top"),sQuery(id+"F22.wireOp",EDGE,"E101.left")])]});
            var Q6;
            Q6=makeQuery(id+"F23.opExtrude","CAP_EDGE",EDGE,{"disambiguationData":[OSD([sQuery(id+"F22.wireOp",EDGE,"E101.right")])],"isStart":false});
            var Q7;
            Q7=makeQuery(id+"F23.opExtrude","CAP_EDGE",EDGE,{"disambiguationData":[OSD([sQuery(id+"F22.wireOp",EDGE,"E101.left")])],"isStart":false});
            chamfer(context, id + "F24", {"entities" : qUnion([Q0, Q1, Q2, Q3, Q4, Q5, Q6, Q7]), "width" : 5 * mm, "tangentPropagation" : true});
        }
        {
            var Q0;
            Q0=makeQuery(id+"F23.opExtrude","SWEPT_BODY",BODY,{"disambiguationData":[OSD([sQuery(id+"F22.wireOp",EDGE,"E101.bottom"),sQuery(id+"F22.wireOp",EDGE,"E101.top"),sQuery(id+"F22.wireOp",EDGE,"E101.left"),sQuery(id+"F22.wireOp",EDGE,"E101.right")])]});
            transform(context, id + "F25", {"entities" : qUnion([Q0]), "transformType" : TransformType.TRANSLATION_3D, "dx" : 116 * mm, "dy" : 0 * mm, "dz" : 0 * mm, "makeCopy" : true});
        }
        {
            var Q0;
            Q0=makeQuery(id+"F23.opExtrude","SWEPT_BODY",BODY,{"disambiguationData":[OSD([sQuery(id+"F22.wireOp",EDGE,"E101.bottom"),sQuery(id+"F22.wireOp",EDGE,"E101.top"),sQuery(id+"F22.wireOp",EDGE,"E101.left"),sQuery(id+"F22.wireOp",EDGE,"E101.right")])]});
            transform(context, id + "F26", {"entities" : qUnion([Q0]), "transformType" : TransformType.TRANSLATION_3D, "dx" : -24 * mm, "dy" : 91 * mm, "dz" : 0 * mm, "makeCopy" : true});
        }
        {
            var Q0;
            Q0=makeQuery(id+"F26.opPattern","COPY",BODY,{"derivedFrom":makeQuery(id+"F23.opExtrude","SWEPT_BODY",BODY,{"disambiguationData":[OSD([sQuery(id+"F22.wireOp",EDGE,"E101.bottom"),sQuery(id+"F22.wireOp",EDGE,"E101.top"),sQuery(id+"F22.wireOp",EDGE,"E101.left"),sQuery(id+"F22.wireOp",EDGE,"E101.right")])]}),"instanceName":"1"});
            transform(context, id + "F27", {"entities" : qUnion([Q0]), "transformType" : TransformType.TRANSLATION_3D, "dx" : 164 * mm, "dy" : 0 * mm, "dz" : 0 * mm, "makeCopy" : true});
        }
        {
            var Q0;
            Q0=qCreatedBy(makeId("Top.planeOp"),FACE);
            var sketch = newSketch(context, id + "F28", { "sketchPlane" : qUnion([Q0])});
            skLineSegment(sketch, "E102.bottom", {"start": v(80.13, 39.6) * mm, "end": v(90.13, 39.6) * mm});
            skLineSegment(sketch, "E102.top", {"start": v(80.13, -24.4) * mm, "end": v(90.13, -24.4) * mm});
            skLineSegment(sketch, "E102.left", {"start": v(80.13, 39.6) * mm, "end": v(80.13, -24.4) * mm});
            skLineSegment(sketch, "E102.right", {"start": v(90.13, 39.6) * mm, "end": v(90.13, -24.4) * mm});
            skLineSegment(sketch, "E103.bottom", {"start": v(189.77, 39.6) * mm, "end": v(199.77, 39.6) * mm});
            skLineSegment(sketch, "E103.top", {"start": v(189.77, -24.4) * mm, "end": v(199.77, -24.4) * mm});
            skLineSegment(sketch, "E103.left", {"start": v(189.77, 39.6) * mm, "end": v(189.77, -24.4) * mm});
            skLineSegment(sketch, "E103.right", {"start": v(199.77, 39.6) * mm, "end": v(199.77, -24.4) * mm});
            skLineSegment(sketch, "E104.bottom", {"start": v(60.13, -24.4) * mm, "end": v(219.77, -24.4) * mm});
            skLineSegment(sketch, "E104.top", {"start": v(60.13, -16.4) * mm, "end": v(219.77, -16.4) * mm});
            skLineSegment(sketch, "E104.left", {"start": v(60.13, -24.4) * mm, "end": v(60.13, -16.4) * mm});
            skLineSegment(sketch, "E104.right", {"start": v(219.77, -24.4) * mm, "end": v(219.77, -16.4) * mm});
            skSolve(sketch);
        }
        {
            var Q0;
            Q0 = qSketchRegion(id + "F28", true);
            extrude(context, id + "F29", {"entities" : qUnion([Q0]), "depth" : 12 * mm, "offsetDistance" : 25 * mm});
        }
        {
            var Q0;
            Q0=makeQuery(id+"F29.opExtrude","SWEPT_BODY",BODY,{"disambiguationData":[OSD([sQuery(id+"F28.wireOp",EDGE,"E102.bottom"),sQuery(id+"F28.wireOp",EDGE,"E102.top"),sQuery(id+"F28.wireOp",EDGE,"E102.left"),sQuery(id+"F28.wireOp",EDGE,"E102.right"),sQuery(id+"F28.wireOp",EDGE,"E103.bottom"),sQuery(id+"F28.wireOp",EDGE,"E103.top"),sQuery(id+"F28.wireOp",EDGE,"E103.left"),sQuery(id+"F28.wireOp",EDGE,"E103.right"),sQuery(id+"F28.wireOp",EDGE,"E104.bottom"),sQuery(id+"F28.wireOp",EDGE,"E104.top"),sQuery(id+"F28.wireOp",EDGE,"E104.left"),sQuery(id+"F28.wireOp",EDGE,"E104.right")])]});
            var Q1;
            Q1=makeQuery(id+"F29.opExtrude","SWEPT_EDGE",EDGE,{"disambiguationData":[OSD([sQuery(id+"F28.wireOp",EDGE,"E104.bottom"),sQuery(id+"F28.wireOp",EDGE,"E104.left")])]});
            transform(context, id + "F30", {"entities" : qUnion([Q0]), "transformType" : TransformType.ROTATION, "transformAxis" : qUnion([Q1]), "angle" : 180 * degree, "makeCopy" : true});
        }
        {
            var Q0;
            Q0=makeQuery(id+"F30.opPattern","COPY",BODY,{"derivedFrom":makeQuery(id+"F29.opExtrude","SWEPT_BODY",BODY,{"disambiguationData":[OSD([sQuery(id+"F28.wireOp",EDGE,"E102.bottom"),sQuery(id+"F28.wireOp",EDGE,"E102.top"),sQuery(id+"F28.wireOp",EDGE,"E102.left"),sQuery(id+"F28.wireOp",EDGE,"E102.right"),sQuery(id+"F28.wireOp",EDGE,"E103.bottom"),sQuery(id+"F28.wireOp",EDGE,"E103.top"),sQuery(id+"F28.wireOp",EDGE,"E103.left"),sQuery(id+"F28.wireOp",EDGE,"E103.right"),sQuery(id+"F28.wireOp",EDGE,"E104.bottom"),sQuery(id+"F28.wireOp",EDGE,"E104.top"),sQuery(id+"F28.wireOp",EDGE,"E104.left"),sQuery(id+"F28.wireOp",EDGE,"E104.right")])]}),"instanceName":"1"});
            transform(context, id + "F31", {"entities" : qUnion([Q0]), "transformType" : TransformType.TRANSLATION_3D, "dx" : 159.5 * mm, "dy" : 0 * mm, "dz" : 0 * mm, "makeCopy" : false});
        }
    });
